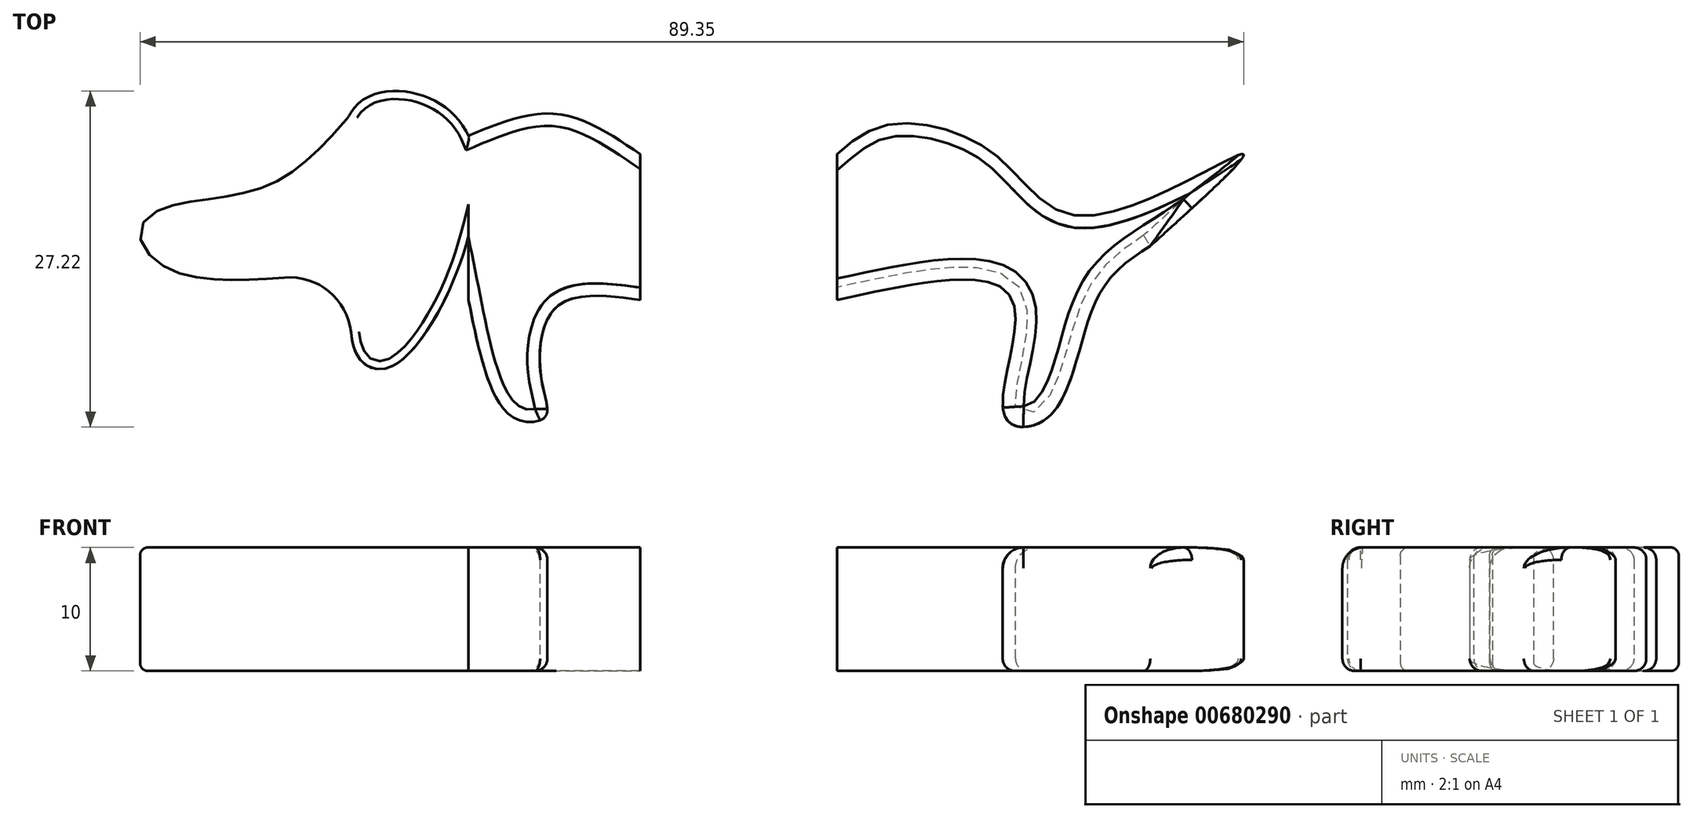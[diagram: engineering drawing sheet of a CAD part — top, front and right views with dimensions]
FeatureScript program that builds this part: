
annotation { "Feature Type Name" : "Feature", "Feature Type Description" : "" }
export const myFeature = defineFeature(function(context is Context, id is Id, definition is map)
    precondition{}
    {
        {
            var Q0;
            Q0=qCreatedBy(makeId("Top.planeOp"),FACE);
            var sketch = newSketch(context, id + "F0", { "sketchPlane" : qUnion([Q0])});
            skFitSpline(sketch, "E0", {"points": [v(-8.27, 9.45) * mm, v(-15.07, 8.86) * mm, v(-16.25, 2.95) * mm, v(-15.96, 0) * mm, v(-18.62, 0) * mm, v(-22.16, 9.45) * mm], "startDerivative": vector(-35.87, 4.8) * mm, "endDerivative": vector(-8.98, 44.94) * mm});
            skFitSpline(sketch, "E1", {"points": [v(-31.91, 11.82) * mm, v(-31.03, 4.73) * mm, v(-27.78, 4.43) * mm, v(-22.16, 22.75) * mm, v(-31.03, 25.41) * mm, v(-31.91, 11.82) * mm]});
            skFitSpline(sketch, "E2", {"points": [v(-31.91, 11.82) * mm, v(-46.1, 11.82) * mm, v(-48.76, 14.77) * mm, v(-46.98, 16.84) * mm, v(-38.71, 18.62) * mm, v(-31.91, 24.22) * mm], "startDerivative": vector(-58.5, -6.83) * mm, "endDerivative": vector(26.81, 30.42) * mm});
            skFitSpline(sketch, "E3", {"points": [v(-22.16, 9.45) * mm, v(-22.16, 14.64) * mm], "startDerivative": vector(0, 5.18) * mm, "endDerivative": vector(0, 5.18) * mm});
            skLineSegment(sketch, "E4", {"start": v(-8.27, 9.45) * mm, "end": v(-8.27, 21.27) * mm});
            skFitSpline(sketch, "E5", {"points": [v(-8.27, 21.27) * mm, v(-15.07, 24.53) * mm, v(-22.16, 22.75) * mm], "startDerivative": vector(-13.29, 8.98) * mm, "endDerivative": vector(-14.5, -6.06) * mm});
            skSolve(sketch);
        }
        {
            var Q0;
            {var subQ0=sQuery(id+"F0.wireOp",EDGE,"E2");Q0=makeQuery(id+"F0.imprint","IMPRINT",FACE,{"disambiguationData":[TD([[makeQuery(id+"F0.imprint","IMPRINT",EDGE,{"derivedFrom":subQ0}),-1.0]])]});}
            var Q1;
            {var subQ0=sQuery(id+"F0.wireOp",EDGE,"E2");var subQ1=sQuery(id+"F0.wireOp",EDGE,"E1");var subQ2=makeQuery(id+"F0.imprint","INTERSECT",VERTEX,{"disambiguationData":[OD(0.0)],"derivedFrom":[subQ1,subQ0]});Q1=makeQuery(id+"F0.imprint","IMPRINT",FACE,{"disambiguationData":[TD([[makeQuery(id+"F0.imprint","IMPRINT",EDGE,{"disambiguationData":[TD([[subQ2,-1.0]])],"derivedFrom":subQ1}),1.0]])]});}
            var Q2;
            Q2=makeQuery(id+"F0.imprint","IMPRINT",FACE,{"disambiguationData":[TD([[makeQuery(id+"F0.imprint","IMPRINT",EDGE,{"derivedFrom":sQuery(id+"F0.wireOp",EDGE,"E0")}),-1.0]])]});
            extrude(context, id + "F1", {"entities" : qUnion([Q0, Q1, Q2]), "depth" : 10 * mm, "offsetDistance" : 25 * mm});
        }
        {
            var Q0;
            Q0=makeQuery(id+"F1.opExtrude","CAP_EDGE",EDGE,{"disambiguationData":[OSD([sQuery(id+"F0.wireOp",EDGE,"E5")])],"isStart":false});
            fillet(context, id + "F2", {"entities" : qUnion([Q0]), "radius" : 1 * mm, "tangentPropagation" : true, "allowEdgeOverflow" : false});
        }
        {
            var Q0;
            {var subQ0=sQuery(id+"F0.wireOp",EDGE,"E5");Q0=makeQuery(id+"F2.opFillet","BLEND_EDGE",EDGE,{"blendedFrom":[makeQuery(id+"F1.opExtrude","CAP_EDGE",EDGE,{"disambiguationData":[OSD([subQ0])],"isStart":false}),makeQuery(id+"F1.opExtrude","CAP_FACE",FACE,{"disambiguationData":[OSD([sQuery(id+"F0.wireOp",EDGE,"E0"),sQuery(id+"F0.wireOp",EDGE,"E1"),sQuery(id+"F0.wireOp",EDGE,"E2"),sQuery(id+"F0.wireOp",EDGE,"E3"),sQuery(id+"F0.wireOp",EDGE,"E4"),subQ0])],"isStart":false})],"blendedInto":[makeQuery(id+"F1.opExtrude","CAP_FACE",FACE,{"disambiguationData":[OSD([sQuery(id+"F0.wireOp",EDGE,"E0"),sQuery(id+"F0.wireOp",EDGE,"E1"),sQuery(id+"F0.wireOp",EDGE,"E2"),sQuery(id+"F0.wireOp",EDGE,"E3"),sQuery(id+"F0.wireOp",EDGE,"E4"),subQ0])],"isStart":false})]});}
            var Q1;
            {var subQ0=sQuery(id+"F0.wireOp",EDGE,"E2");var subQ1=sQuery(id+"F0.wireOp",EDGE,"E1");Q1=makeQuery(id+"F1.opExtrude","SWEPT_EDGE",EDGE,{"disambiguationData":[OSD([subQ1,subQ0]),TDD([makeQuery(id+"F0.imprint","INTERSECT",VERTEX,{"disambiguationData":[OD(0.0)],"derivedFrom":[subQ1,subQ0]})])]});}
            var Q2;
            {var subQ0=sQuery(id+"F0.wireOp",EDGE,"E2");var subQ1=sQuery(id+"F0.wireOp",EDGE,"E1");Q2=makeQuery(id+"F1.opExtrude","SWEPT_EDGE",EDGE,{"disambiguationData":[OSD([subQ1,subQ0]),TDD([makeQuery(id+"F0.imprint","INTERSECT",VERTEX,{"disambiguationData":[OD(1.0)],"derivedFrom":[subQ1,subQ0]})])]});}
            fillet(context, id + "F3", {"entities" : qUnion([Q0, Q1, Q2]), "radius" : 5 * mm, "tangentPropagation" : true, "allowEdgeOverflow" : false});
        }
        {
            var Q0;
            Q0=makeQuery(id+"F1.opExtrude","CAP_EDGE",EDGE,{"disambiguationData":[OSD([sQuery(id+"F0.wireOp",EDGE,"E5")])],"isStart":true});
            fillet(context, id + "F4", {"entities" : qUnion([Q0]), "radius" : 1 * mm, "tangentPropagation" : true, "allowEdgeOverflow" : false});
        }
        {
            var Q0;
            Q0=qCreatedBy(makeId("Top.planeOp"),FACE);
            var sketch = newSketch(context, id + "F5", { "sketchPlane" : qUnion([Q0])});
            skLineSegment(sketch, "E6", {"start": v(7.68, 21.27) * mm, "end": v(7.68, 9.45) * mm});
            skFitSpline(sketch, "E7", {"points": [v(7.68, 21.27) * mm, v(11.82, 23.64) * mm, v(20.39, 21.27) * mm, v(27.78, 16.25) * mm, v(40.48, 21.27) * mm, v(33.1, 13.89) * mm], "startDerivative": vector(24.28, 21.1) * mm, "endDerivative": vector(-57.61, -51.9) * mm});
            skFitSpline(sketch, "E8", {"points": [v(33.1, 13.89) * mm, v(28.66, 9.45) * mm, v(24.82, 0) * mm, v(21.28, 0) * mm, v(21.87, 9.45) * mm, v(7.68, 9.45) * mm], "startDerivative": vector(-28.99, -18.89) * mm, "endDerivative": vector(-74.37, -16.46) * mm});
            skSolve(sketch);
        }
        {
            var Q0;
            Q0=makeQuery(id+"F5.imprint","IMPRINT",FACE,{"disambiguationData":[TD([[makeQuery(id+"F5.imprint","IMPRINT",EDGE,{"derivedFrom":sQuery(id+"F5.wireOp",EDGE,"E6")}),1.0]])]});
            extrude(context, id + "F6", {"entities" : qUnion([Q0]), "depth" : 10 * mm, "offsetDistance" : 25 * mm});
        }
        {
            var Q0;
            Q0=makeQuery(id+"F6.opExtrude","CAP_EDGE",EDGE,{"disambiguationData":[OSD([sQuery(id+"F5.wireOp",EDGE,"E8")])],"isStart":false});
            fillet(context, id + "F7", {"entities" : qUnion([Q0]), "radius" : 1.69 * mm, "tangentPropagation" : true, "allowEdgeOverflow" : false});
        }
        {
            var Q0;
            Q0=makeQuery(id+"F6.opExtrude","CAP_EDGE",EDGE,{"disambiguationData":[OSD([sQuery(id+"F5.wireOp",EDGE,"E8")])],"isStart":true});
            fillet(context, id + "F8", {"entities" : qUnion([Q0]), "radius" : 1 * mm, "tangentPropagation" : true, "allowEdgeOverflow" : false});
        }
        {
            var Q0;
            Q0=makeQuery(id+"F6.opExtrude","CAP_EDGE",EDGE,{"disambiguationData":[OSD([sQuery(id+"F5.wireOp",EDGE,"E7")])],"isStart":false});
            fillet(context, id + "F9", {"entities" : qUnion([Q0]), "radius" : 1 * mm, "tangentPropagation" : true, "allowEdgeOverflow" : false});
        }
        {
            var Q0;
            Q0=makeQuery(id+"F1.opExtrude","CAP_EDGE",EDGE,{"disambiguationData":[OSD([sQuery(id+"F0.wireOp",EDGE,"E0")])],"isStart":true});
            fillet(context, id + "F10", {"entities" : qUnion([Q0]), "radius" : 1 * mm, "tangentPropagation" : true, "allowEdgeOverflow" : false});
        }
        {
            var Q0;
            Q0=makeQuery(id+"F1.opExtrude","CAP_EDGE",EDGE,{"disambiguationData":[OSD([sQuery(id+"F0.wireOp",EDGE,"E0")])],"isStart":false});
            fillet(context, id + "F11", {"entities" : qUnion([Q0]), "radius" : 1 * mm, "tangentPropagation" : true, "allowEdgeOverflow" : false});
        }
        {
            var Q0;
            {var subQ0=sQuery(id+"F0.wireOp",EDGE,"E1");Q0=makeQuery(id+"F1.opExtrude","CAP_EDGE",EDGE,{"disambiguationData":[OSD([subQ0]),TDD([makeQuery(id+"F0.imprint","IMPRINT",EDGE,{"disambiguationData":[TD([[makeQuery(id+"F0.imprint","INTERSECT",VERTEX,{"disambiguationData":[OD(0.0)],"derivedFrom":[subQ0,sQuery(id+"F0.wireOp",EDGE,"E2")]}),-1.0]])],"derivedFrom":subQ0})])],"isStart":false});}
            fillet(context, id + "F12", {"entities" : qUnion([Q0]), "radius" : 0.65 * mm, "tangentPropagation" : true, "allowEdgeOverflow" : false});
        }
        {
            var Q0;
            {var subQ0=sQuery(id+"F0.wireOp",EDGE,"E1");Q0=makeQuery(id+"F1.opExtrude","CAP_EDGE",EDGE,{"disambiguationData":[OSD([subQ0]),TDD([makeQuery(id+"F0.imprint","IMPRINT",EDGE,{"disambiguationData":[TD([[makeQuery(id+"F0.imprint","INTERSECT",VERTEX,{"disambiguationData":[OD(1.0)],"derivedFrom":[subQ0,sQuery(id+"F0.wireOp",EDGE,"E2")]}),1.0]])],"derivedFrom":subQ0})])],"isStart":true});}
            fillet(context, id + "F13", {"entities" : qUnion([Q0]), "radius" : 0.65 * mm, "tangentPropagation" : true, "allowEdgeOverflow" : false});
        }
    });
